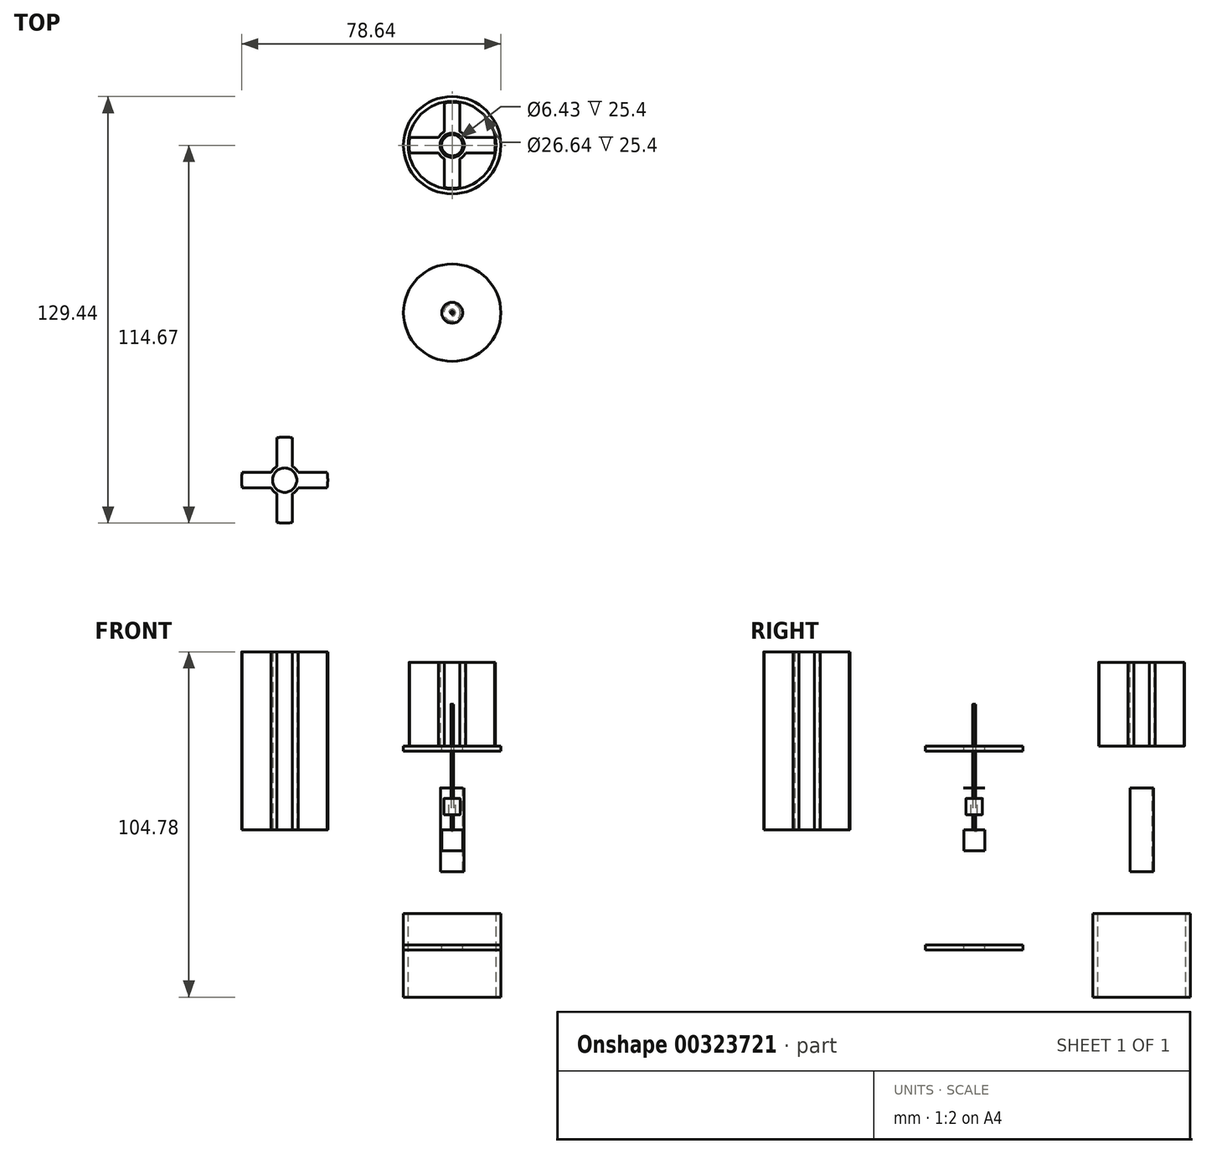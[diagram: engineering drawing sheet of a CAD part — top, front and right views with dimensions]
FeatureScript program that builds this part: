
annotation { "Feature Type Name" : "Feature", "Feature Type Description" : "" }
export const myFeature = defineFeature(function(context is Context, id is Id, definition is map)
    precondition{}
    {
        {
            assignVariable(context, id + "F0", {"name" : "emtY", "anyValue" : 50.8 * mm});
        }
        {
            assignVariable(context, id + "F1", {"name" : "emtLen", "anyValue" : 25.4 * mm});
        }
        {
            var Q0;
            Q0=qCreatedBy(makeId("Top.planeOp"),FACE);
            var sketch = newSketch(context, id + "F2", { "sketchPlane" : qUnion([Q0])});
            skCircle(sketch, "E0", {"center": v(0, 0) * mm, "radius": 14.77 * mm});
            skCircle(sketch, "E1", {"center": v(0, 0) * mm, "radius": 13.32 * mm});
            skSolve(sketch);
        }
        {
            var Q0;
            Q0=makeQuery(id+"F2.imprint","IMPRINT",FACE,{"disambiguationData":[TD([[makeQuery(id+"F2.imprint","IMPRINT",EDGE,{"derivedFrom":sQuery(id+"F2.wireOp",EDGE,"E0")}),1.0]])]});
            extrude(context, id + "F3", {"entities" : qUnion([Q0]), "oppositeDirection" : true, "depth" : 25.4 * mm});
        }
        {
            var Q0;
            Q0=makeQuery(id+"F3.opExtrude","SWEPT_BODY",BODY,{"disambiguationData":[OSD([sQuery(id+"F2.wireOp",EDGE,"E0"),sQuery(id+"F2.wireOp",EDGE,"E1")])]});
            transform(context, id + "F4", {"entities" : qUnion([Q0]), "transformType" : TransformType.TRANSLATION_3D, "dx" : 0 * mm, "dy" : getVariable(context, 'emtY'), "dz" : -25.4 * mm, "makeCopy" : false});
        }
        {
            var Q0;
            Q0=qCreatedBy(makeId("Top.planeOp"),FACE);
            var sketch = newSketch(context, id + "F5", { "sketchPlane" : qUnion([Q0])});
            skCircle(sketch, "E2", {"center": v(0, 0) * mm, "radius": 3.57 * mm});
            skCircle(sketch, "E3", {"center": v(0, 0) * mm, "radius": 3.22 * mm});
            skSolve(sketch);
        }
        {
            var Q0;
            Q0 = qSketchRegion(id + "F5", true);
            extrude(context, id + "F6", {"entities" : qUnion([Q0]), "oppositeDirection" : true, "depth" : (getVariable(context, 'emtLen'))});
        }
        {
            var Q0;
            Q0=makeQuery(id+"F6.opExtrude","SWEPT_BODY",BODY,{"disambiguationData":[OSD([sQuery(id+"F5.wireOp",EDGE,"E2"),sQuery(id+"F5.wireOp",EDGE,"E3")])]});
            transform(context, id + "F7", {"entities" : qUnion([Q0]), "transformType" : TransformType.TRANSLATION_3D, "dx" : 0 * mm, "dy" : 50.8 * mm, "dz" : 12.7 * mm, "makeCopy" : false});
        }
        {
            assignVariable(context, id + "F8", {"name" : "bushingLen", "anyValue" : 3 / 812.8 * mm});
        }
        {
            var Q0;
            Q0=qCreatedBy(makeId("Top.planeOp"),FACE);
            var sketch = newSketch(context, id + "F9", { "sketchPlane" : qUnion([Q0])});
            skCircle(sketch, "E4", {"center": v(0, 0) * mm, "radius": 3.22 * mm});
            skCircle(sketch, "E5", {"center": v(0, 0) * mm, "radius": 0.44 * mm});
            skSolve(sketch);
        }
        {
            var Q0;
            Q0=makeQuery(id+"F9.imprint","IMPRINT",FACE,{"disambiguationData":[TD([[makeQuery(id+"F9.imprint","IMPRINT",EDGE,{"derivedFrom":sQuery(id+"F9.wireOp",EDGE,"E4")}),1.0]])]});
            extrude(context, id + "F10", {"entities" : qUnion([Q0]), "oppositeDirection" : true, "depth" : getVariable(context, 'bushingLen')});
        }
        {
            var Q0;
            Q0=makeQuery(id+"F10.opExtrude","SWEPT_BODY",BODY,{"disambiguationData":[OSD([sQuery(id+"F9.wireOp",EDGE,"E4"),sQuery(id+"F9.wireOp",EDGE,"E5")])]});
            transform(context, id + "F11", {"entities" : qUnion([Q0]), "transformType" : TransformType.TRANSLATION_3D, "dx" : 0 * mm, "dy" : 0 * mm, "dz" : 12.7 * mm, "makeCopy" : false});
        }
        {
            var Q0;
            Q0=qCreatedBy(makeId("Top.planeOp"),FACE);
            var sketch = newSketch(context, id + "F12", { "sketchPlane" : qUnion([Q0])});
            skCircle(sketch, "E6", {"center": v(0, 0) * mm, "radius": 3.7 * mm});
            skCircle(sketch, "E7", {"center": v(0, 0) * mm, "radius": 4.76 * mm});
            skLineSegment(sketch, "E8", {"start": v(-2.38, 12.85) * mm, "end": v(-2.38, 4.12) * mm});
            skLineSegment(sketch, "E9", {"start": v(2.38, 12.85) * mm, "end": v(2.38, 4.12) * mm});
            skLineSegment(sketch, "E10", {"start": v(4.12, 2.38) * mm, "end": v(12.85, 2.38) * mm});
            skLineSegment(sketch, "E11", {"start": v(4.12, -2.38) * mm, "end": v(12.85, -2.38) * mm});
            skLineSegment(sketch, "E12", {"start": v(2.38, -4.12) * mm, "end": v(2.38, -12.85) * mm});
            skLineSegment(sketch, "E13", {"start": v(-2.38, -4.12) * mm, "end": v(-2.38, -12.85) * mm});
            skLineSegment(sketch, "E14", {"start": v(-12.97, 2.38) * mm, "end": v(-4.12, 2.38) * mm});
            skLineSegment(sketch, "E15", {"start": v(-12.85, -2.38) * mm, "end": v(-4.12, -2.38) * mm});
            skCircle(sketch, "E16", {"center": v(0, 0) * mm, "radius": 13.07 * mm});
            skSolve(sketch);
        }
        {
            var Q0;
            {var subQ0=sQuery(id+"F12.wireOp",EDGE,"E12");Q0=makeQuery(id+"F12.imprint","IMPRINT",FACE,{"disambiguationData":[TD([[makeQuery(id+"F12.imprint","IMPRINT",EDGE,{"derivedFrom":subQ0}),-1.0]])]});}
            var Q1;
            {var subQ0=sQuery(id+"F12.wireOp",EDGE,"E14");Q1=makeQuery(id+"F12.imprint","IMPRINT",FACE,{"disambiguationData":[TD([[makeQuery(id+"F12.imprint","IMPRINT",EDGE,{"derivedFrom":subQ0}),-1.0]])]});}
            var Q2;
            {var subQ0=sQuery(id+"F12.wireOp",EDGE,"E8");Q2=makeQuery(id+"F12.imprint","IMPRINT",FACE,{"disambiguationData":[TD([[makeQuery(id+"F12.imprint","IMPRINT",EDGE,{"derivedFrom":subQ0}),1.0]])]});}
            var Q3;
            {var subQ0=sQuery(id+"F12.wireOp",EDGE,"E10");Q3=makeQuery(id+"F12.imprint","IMPRINT",FACE,{"disambiguationData":[TD([[makeQuery(id+"F12.imprint","IMPRINT",EDGE,{"derivedFrom":subQ0}),-1.0]])]});}
            var Q4;
            Q4=makeQuery(id+"F12.imprint","IMPRINT",FACE,{"disambiguationData":[TD([[makeQuery(id+"F12.imprint","IMPRINT",EDGE,{"derivedFrom":sQuery(id+"F12.wireOp",EDGE,"E6")}),-1.0]])]});
            extrude(context, id + "F13", {"entities" : qUnion([Q0, Q1, Q2, Q3, Q4]), "depth" : (getVariable(context, 'emtLen')) * 1});
        }
        {
            var Q0;
            Q0=makeQuery(id+"F13.opExtrude","SWEPT_BODY",BODY,{"disambiguationData":[OSD([sQuery(id+"F12.wireOp",EDGE,"E6"),sQuery(id+"F12.wireOp",EDGE,"E7"),sQuery(id+"F12.wireOp",EDGE,"E8"),sQuery(id+"F12.wireOp",EDGE,"E9"),sQuery(id+"F12.wireOp",EDGE,"E10"),sQuery(id+"F12.wireOp",EDGE,"E11"),sQuery(id+"F12.wireOp",EDGE,"E12"),sQuery(id+"F12.wireOp",EDGE,"E13"),sQuery(id+"F12.wireOp",EDGE,"E14"),sQuery(id+"F12.wireOp",EDGE,"E15"),sQuery(id+"F12.wireOp",EDGE,"E16")])]});
            transform(context, id + "F14", {"entities" : qUnion([Q0]), "transformType" : TransformType.TRANSLATION_3D, "dx" : 0 * mm, "dy" : getVariable(context, 'emtY'), "dz" : 25.4 * mm, "makeCopy" : false});
        }
        {
            var Q0;
            Q0=qCreatedBy(makeId("Top.planeOp"),FACE);
            var sketch = newSketch(context, id + "F15", { "sketchPlane" : qUnion([Q0])});
            skCircle(sketch, "E17", {"center": v(0, 0) * mm, "radius": 2.5 * mm});
            skCircle(sketch, "E18", {"center": v(0, 0) * mm, "radius": 1 * mm});
            skSolve(sketch);
        }
        {
            var Q0;
            Q0=makeQuery(id+"F15.imprint","IMPRINT",FACE,{"disambiguationData":[TD([[makeQuery(id+"F15.imprint","IMPRINT",EDGE,{"derivedFrom":sQuery(id+"F15.wireOp",EDGE,"E17")}),1.0]])]});
            extrude(context, id + "F16", {"entities" : qUnion([Q0]), "oppositeDirection" : true, "depth" : 5 * mm});
        }
        {
            var Q0;
            Q0=makeQuery(id+"F16.opExtrude","CAP_EDGE",EDGE,{"disambiguationData":[OSD([sQuery(id+"F15.wireOp",EDGE,"E17")])],"isStart":false});
            fillet(context, id + "F17", {"entities" : qUnion([Q0]), "radius" : .15 * mm, "tangentPropagation" : true, "allowEdgeOverflow" : false});
        }
        {
            var Q0;
            Q0=makeQuery(id+"F16.opExtrude","CAP_EDGE",EDGE,{"disambiguationData":[OSD([sQuery(id+"F15.wireOp",EDGE,"E17")])],"isStart":true});
            fillet(context, id + "F18", {"entities" : qUnion([Q0]), "radius" : .15 * mm, "tangentPropagation" : true, "allowEdgeOverflow" : false});
        }
        {
            var Q0;
            Q0=makeQuery(id+"F16.opExtrude","SWEPT_BODY",BODY,{"disambiguationData":[OSD([sQuery(id+"F15.wireOp",EDGE,"E17"),sQuery(id+"F15.wireOp",EDGE,"E18")])]});
            transform(context, id + "F19", {"entities" : qUnion([Q0]), "transformType" : TransformType.TRANSLATION_3D, "dx" : 0 * mm, "dy" : 0 * mm, "dz" : 9.52 * mm, "makeCopy" : false});
        }
        {
            assignVariable(context, id + "F20", {"name" : "rearBearingLen", "anyValue" : 6.35 * mm});
        }
        {
            var Q0;
            Q0=qCreatedBy(makeId("Top.planeOp"),FACE);
            var sketch = newSketch(context, id + "F21", { "sketchPlane" : qUnion([Q0])});
            skCircle(sketch, "E19", {"center": v(0, 0) * mm, "radius": 3.18 * mm});
            skSolve(sketch);
        }
        {
            var Q0;
            Q0=makeQuery(id+"F21.imprint","IMPRINT",FACE,{"disambiguationData":[TD([[makeQuery(id+"F21.imprint","IMPRINT",EDGE,{"derivedFrom":sQuery(id+"F21.wireOp",EDGE,"E19")}),1.0]])]});
            extrude(context, id + "F22", {"entities" : qUnion([Q0]), "oppositeDirection" : true, "depth" : (getVariable(context, 'rearBearingLen'))});
        }
        {
            var Q0;
            Q0=qCreatedBy(makeId("Front.planeOp"),FACE);
            var sketch = newSketch(context, id + "F23", { "sketchPlane" : qUnion([Q0])});
            skPoint(sketch, "E20", {"position": v(0, 0) * mm});
            skSolve(sketch);
        }
        {
            var Q0;
            Q0=sQuery(id+"F23.wireOp",VERTEX,"E20");
            var Q1;
            Q1=makeQuery(id+"F22.opExtrude","SWEPT_BODY",BODY,{"disambiguationData":[OSD([sQuery(id+"F21.wireOp",EDGE,"E19")])]});
            hole(context, id + "F24", {"style" : HoleStyle.SIMPLE, "endStyle" : HoleEndStyle.BLIND, "holeDiameter" : 0.84 * mm, "holeDepth" : 0.84 * mm, "tappedDepth" : 12.7 * mm, "tapClearance" : 3, "locations" : qUnion([Q0]), "scope" : qUnion([Q1]), "startStyle" : HoleStartStyle.SKETCH});
        }
        {
            var Q0;
            Q0=qCreatedBy(makeId("Top.planeOp"),FACE);
            var sketch = newSketch(context, id + "F25", { "sketchPlane" : qUnion([Q0])});
            skCircle(sketch, "E21", {"center": v(0, 0) * mm, "radius": 0.4 * mm});
            skSolve(sketch);
        }
        {
            assignVariable(context, id + "F26", {"name" : "shaftLen", "anyValue" : 38.1 * mm});
        }
        {
            var Q0;
            Q0 = qSketchRegion(id + "F25", true);
            extrude(context, id + "F27", {"entities" : qUnion([Q0]), "depth" : getVariable(context, 'shaftLen')});
        }
        {
            var Q0;
            Q0=qCreatedBy(makeId("Top.planeOp"),FACE);
            var sketch = newSketch(context, id + "F28", { "sketchPlane" : qUnion([Q0])});
            skCircle(sketch, "E22", {"center": v(0, 0) * mm, "radius": 14.77 * mm});
            skCircle(sketch, "E23", {"center": v(0, 0) * mm, "radius": 3.18 * mm});
            skSolve(sketch);
        }
        {
            var Q0;
            Q0=makeQuery(id+"F28.imprint","IMPRINT",FACE,{"disambiguationData":[TD([[makeQuery(id+"F28.imprint","IMPRINT",EDGE,{"derivedFrom":sQuery(id+"F28.wireOp",EDGE,"E22")}),1.0]])]});
            var Q1;
            Q1=makeQuery(id+"F28.imprint","IMPRINT",FACE,{"disambiguationData":[TD([[makeQuery(id+"F28.imprint","IMPRINT",EDGE,{"derivedFrom":sQuery(id+"F28.wireOp",EDGE,"c8Trr1LJ-R9Xv-jelW-un3X-HdYb6hQ7cFNu")}),1.0]])]});
            extrude(context, id + "F29", {"entities" : qUnion([Q0, Q1]), "oppositeDirection" : true, "depth" : 1.57 * mm});
        }
        {
            var Q0;
            Q0=makeQuery(id+"F29.opExtrude","SWEPT_BODY",BODY,{"disambiguationData":[OSD([sQuery(id+"F28.wireOp",EDGE,"E22"),sQuery(id+"F28.wireOp",EDGE,"E23")])]});
            transform(context, id + "F30", {"entities" : qUnion([Q0]), "transformType" : TransformType.TRANSLATION_3D, "dx" : 0 * mm, "dy" : 0 * mm, "dz" : -34.92 * mm, "makeCopy" : false});
        }
        {
            var Q0;
            Q0=qCreatedBy(makeId("Top.planeOp"),FACE);
            var sketch = newSketch(context, id + "F31", { "sketchPlane" : qUnion([Q0])});
            skCircle(sketch, "E24", {"center": v(0, 0) * mm, "radius": 14.77 * mm});
            skCircle(sketch, "E25", {"center": v(0, 0) * mm, "radius": 3.18 * mm});
            skSolve(sketch);
        }
        {
            var Q0;
            Q0=makeQuery(id+"F31.imprint","IMPRINT",FACE,{"disambiguationData":[TD([[makeQuery(id+"F31.imprint","IMPRINT",EDGE,{"derivedFrom":sQuery(id+"F31.wireOp",EDGE,"E24")}),1.0]])]});
            extrude(context, id + "F32", {"entities" : qUnion([Q0]), "oppositeDirection" : true, "depth" : 1.59 * mm});
        }
        {
            var Q0;
            Q0=makeQuery(id+"F32.opExtrude","SWEPT_BODY",BODY,{"disambiguationData":[OSD([sQuery(id+"F31.wireOp",EDGE,"E24"),sQuery(id+"F31.wireOp",EDGE,"E25")])]});
            transform(context, id + "F33", {"entities" : qUnion([Q0]), "transformType" : TransformType.TRANSLATION_3D, "dx" : 0 * mm, "dy" : 0 * mm, "dz" : 25.4 * mm, "makeCopy" : false});
        }
        {
            var Q0;
            Q0=qCreatedBy(makeId("Top.planeOp"),FACE);
            var sketch = newSketch(context, id + "F34", { "sketchPlane" : qUnion([Q0])});
            skCircle(sketch, "E26", {"center": v(0, 0) * mm, "radius": 3.7 * mm});
            skCircle(sketch, "E27", {"center": v(0, 0) * mm, "radius": 4.76 * mm});
            skLineSegment(sketch, "E28", {"start": v(-2.38, 12.85) * mm, "end": v(-2.38, 4.12) * mm});
            skLineSegment(sketch, "E29", {"start": v(2.38, 12.85) * mm, "end": v(2.38, 4.12) * mm});
            skLineSegment(sketch, "E30", {"start": v(4.12, -2.38) * mm, "end": v(12.85, -2.38) * mm});
            skLineSegment(sketch, "E31", {"start": v(2.38, -4.12) * mm, "end": v(2.38, -12.85) * mm});
            skLineSegment(sketch, "E32", {"start": v(-2.38, -4.12) * mm, "end": v(-2.38, -12.85) * mm});
            skLineSegment(sketch, "E33", {"start": v(-12.85, 2.38) * mm, "end": v(-4.12, 2.38) * mm});
            skLineSegment(sketch, "E34", {"start": v(-12.85, -2.38) * mm, "end": v(-4.12, -2.38) * mm});
            skCircle(sketch, "E35", {"center": v(0, 0) * mm, "radius": 13.07 * mm});
            skLineSegment(sketch, "E36", {"start": v(4.12, 2.38) * mm, "end": v(12.85, 2.38) * mm});
            skSolve(sketch);
        }
        {
            var Q0;
            Q0=makeQuery(id+"F34.imprint","IMPRINT",FACE,{"disambiguationData":[TD([[makeQuery(id+"F34.imprint","IMPRINT",EDGE,{"derivedFrom":sQuery(id+"F34.wireOp",EDGE,"E26")}),-1.0]])]});
            var Q1;
            {var subQ0=sQuery(id+"F34.wireOp",EDGE,"E28");Q1=makeQuery(id+"F34.imprint","IMPRINT",FACE,{"disambiguationData":[TD([[makeQuery(id+"F34.imprint","IMPRINT",EDGE,{"derivedFrom":subQ0}),1.0]])]});}
            var Q2;
            {var subQ0=sQuery(id+"F34.wireOp",EDGE,"E30");Q2=makeQuery(id+"F34.imprint","IMPRINT",FACE,{"disambiguationData":[TD([[makeQuery(id+"F34.imprint","IMPRINT",EDGE,{"derivedFrom":subQ0}),1.0]])]});}
            var Q3;
            {var subQ0=sQuery(id+"F34.wireOp",EDGE,"E33");Q3=makeQuery(id+"F34.imprint","IMPRINT",FACE,{"disambiguationData":[TD([[makeQuery(id+"F34.imprint","IMPRINT",EDGE,{"derivedFrom":subQ0}),-1.0]])]});}
            var Q4;
            {var subQ0=sQuery(id+"F34.wireOp",EDGE,"E31");Q4=makeQuery(id+"F34.imprint","IMPRINT",FACE,{"disambiguationData":[TD([[makeQuery(id+"F34.imprint","IMPRINT",EDGE,{"derivedFrom":subQ0}),-1.0]])]});}
            extrude(context, id + "F35", {"entities" : qUnion([Q0, Q1, Q2, Q3, Q4]), "depth" : 53.97 * mm});
        }
        {
            var Q0;
            Q0=makeQuery(id+"F35.opExtrude","SWEPT_BODY",BODY,{"disambiguationData":[OSD([sQuery(id+"F34.wireOp",EDGE,"E26"),sQuery(id+"F34.wireOp",EDGE,"E27"),sQuery(id+"F34.wireOp",EDGE,"E28"),sQuery(id+"F34.wireOp",EDGE,"E29"),sQuery(id+"F34.wireOp",EDGE,"E30"),sQuery(id+"F34.wireOp",EDGE,"E31"),sQuery(id+"F34.wireOp",EDGE,"E32"),sQuery(id+"F34.wireOp",EDGE,"E33"),sQuery(id+"F34.wireOp",EDGE,"E34"),sQuery(id+"F34.wireOp",EDGE,"E35"),sQuery(id+"F34.wireOp",EDGE,"E36")])]});
            transform(context, id + "F36", {"entities" : qUnion([Q0]), "transformType" : TransformType.TRANSLATION_3D, "dx" : -50.8 * mm, "dy" : -50.8 * mm, "dz" : 0 * mm, "makeCopy" : false});
        }
    });
